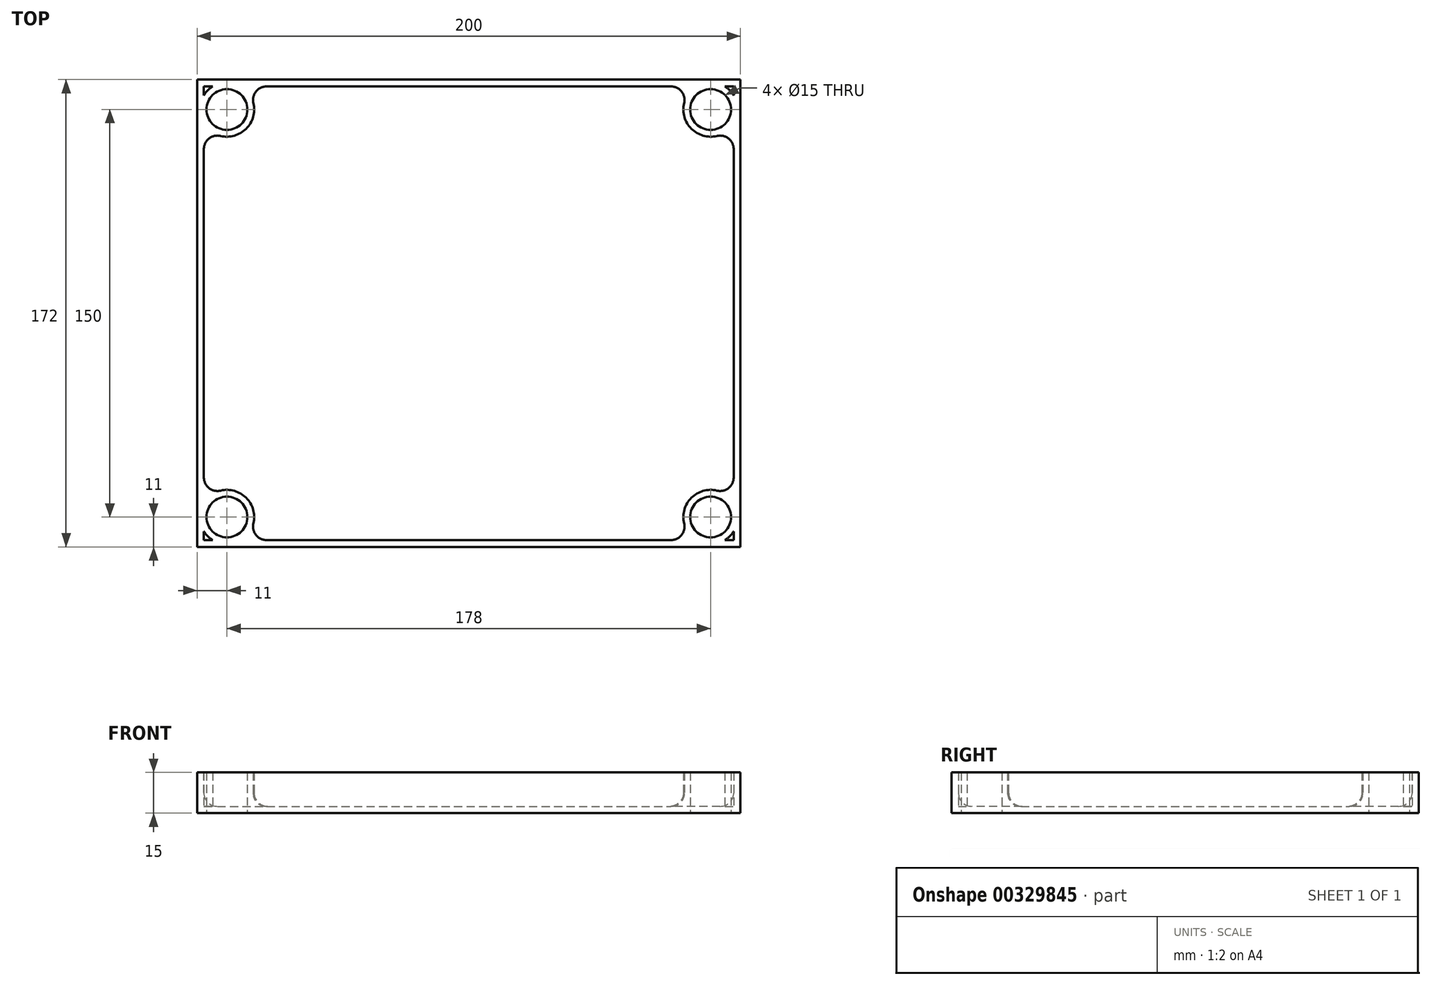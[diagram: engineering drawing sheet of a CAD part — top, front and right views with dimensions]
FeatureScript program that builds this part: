
annotation { "Feature Type Name" : "Feature", "Feature Type Description" : "" }
export const myFeature = defineFeature(function(context is Context, id is Id, definition is map)
    precondition{}
    {
        {
            var Q0;
            Q0=qCreatedBy(makeId("Top.planeOp"),FACE);
            var sketch = newSketch(context, id + "F0", { "sketchPlane" : qUnion([Q0])});
            skLineSegment(sketch, "E0.bottom", {"start": v(0, 0) * mm, "end": v(200, 0) * mm});
            skLineSegment(sketch, "E0.top", {"start": v(0, 172) * mm, "end": v(200, 172) * mm});
            skLineSegment(sketch, "E0.left", {"start": v(0, 0) * mm, "end": v(0, 172) * mm});
            skLineSegment(sketch, "E0.right", {"start": v(200, 0) * mm, "end": v(200, 172) * mm});
            skCircle(sketch, "E1", {"center": v(11, 11) * mm, "radius": 7.5 * mm});
            skCircle(sketch, "E2.0.1.0", {"center": v(11, 161) * mm, "radius": 7.5 * mm});
            skCircle(sketch, "E2.1.0.0", {"center": v(189, 11) * mm, "radius": 7.5 * mm});
            skCircle(sketch, "E2.1.1.0", {"center": v(189, 161) * mm, "radius": 7.5 * mm});
            skLineSegment(sketch, "E2.direction1", {"start": v(11, 11) * mm, "end": v(189, 11) * mm, "construction": true});
            skLineSegment(sketch, "E2.direction2", {"start": v(11, 11) * mm, "end": v(11, 161) * mm, "construction": true});
            skLineSegment(sketch, "E3", {"start": v(0, 11) * mm, "end": v(11, 11) * mm, "construction": true});
            skLineSegment(sketch, "E4", {"start": v(11, 11) * mm, "end": v(11, 0) * mm, "construction": true});
            skLineSegment(sketch, "E5", {"start": v(189, 172) * mm, "end": v(189, 161) * mm, "construction": true});
            skLineSegment(sketch, "E6", {"start": v(189, 161) * mm, "end": v(200, 161) * mm, "construction": true});
            skSolve(sketch);
        }
        {
            var Q0;
            Q0=makeQuery(id+"F0.imprint","IMPRINT",FACE,{"disambiguationData":[TD([[makeQuery(id+"F0.imprint","IMPRINT",EDGE,{"derivedFrom":sQuery(id+"F0.wireOp",EDGE,"E0.bottom")}),1.0]])]});
            extrude(context, id + "F1", {"entities" : qUnion([Q0]), "depth" : 15 * mm, "offsetDistance" : 25 * mm});
        }
        {
            var Q0;
            Q0=makeQuery(id+"F1.opExtrude","CAP_FACE",FACE,{"disambiguationData":[OSD([sQuery(id+"F0.wireOp",EDGE,"E0.bottom"),sQuery(id+"F0.wireOp",EDGE,"E0.top"),sQuery(id+"F0.wireOp",EDGE,"E0.left"),sQuery(id+"F0.wireOp",EDGE,"E0.right"),sQuery(id+"F0.wireOp",EDGE,"E1"),sQuery(id+"F0.wireOp",EDGE,"E2.0.1.0"),sQuery(id+"F0.wireOp",EDGE,"E2.1.0.0"),sQuery(id+"F0.wireOp",EDGE,"E2.1.1.0")])],"isStart":false});
            shell(context, id + "F2", {"entities" : qUnion([Q0]), "thickness" : 2.5 * mm});
        }
        {
            var Q0;
            {var subQ0=sQuery(id+"F0.wireOp",EDGE,"E2.0.1.0");Q0=makeQuery(id+"F2.opShell","OFFSET_EDGE",EDGE,{"disambiguationData":[OSD([subQ0]),TDD([makeQuery(id+"F1.opExtrude","CAP_EDGE",EDGE,{"disambiguationData":[OSD([subQ0])],"isStart":true})]),OD(0.0)]});}
            var Q1;
            {var subQ0=sQuery(id+"F0.wireOp",EDGE,"E2.1.1.0");Q1=makeQuery(id+"F2.opShell","OFFSET_EDGE",EDGE,{"disambiguationData":[OSD([subQ0]),TDD([makeQuery(id+"F1.opExtrude","CAP_EDGE",EDGE,{"disambiguationData":[OSD([subQ0])],"isStart":true})]),OD(0.0)]});}
            var Q2;
            {var subQ0=sQuery(id+"F0.wireOp",EDGE,"E2.1.0.0");Q2=makeQuery(id+"F2.opShell","OFFSET_EDGE",EDGE,{"disambiguationData":[OSD([subQ0]),TDD([makeQuery(id+"F1.opExtrude","CAP_EDGE",EDGE,{"disambiguationData":[OSD([subQ0])],"isStart":true})]),OD(0.0)]});}
            var Q3;
            {var subQ0=sQuery(id+"F0.wireOp",EDGE,"E1");Q3=makeQuery(id+"F2.opShell","OFFSET_EDGE",EDGE,{"disambiguationData":[OSD([subQ0]),TDD([makeQuery(id+"F1.opExtrude","CAP_EDGE",EDGE,{"disambiguationData":[OSD([subQ0])],"isStart":true})]),OD(0.0)]});}
            var Q4;
            {var subQ0=sQuery(id+"F0.wireOp",EDGE,"E0.bottom");Q4=makeQuery(id+"F2.opShell","OFFSET_EDGE",EDGE,{"disambiguationData":[OSD([subQ0]),TDD([makeQuery(id+"F1.opExtrude","CAP_EDGE",EDGE,{"disambiguationData":[OSD([subQ0])],"isStart":true})]),OD(2.0)]});}
            var Q5;
            {var subQ0=sQuery(id+"F0.wireOp",EDGE,"E0.left");Q5=makeQuery(id+"F2.opShell","OFFSET_EDGE",EDGE,{"disambiguationData":[OSD([subQ0]),TDD([makeQuery(id+"F1.opExtrude","CAP_EDGE",EDGE,{"disambiguationData":[OSD([subQ0])],"isStart":true})]),OD(2.0)]});}
            var Q6;
            {var subQ0=sQuery(id+"F0.wireOp",EDGE,"E0.top");Q6=makeQuery(id+"F2.opShell","OFFSET_EDGE",EDGE,{"disambiguationData":[OSD([subQ0]),TDD([makeQuery(id+"F1.opExtrude","CAP_EDGE",EDGE,{"disambiguationData":[OSD([subQ0])],"isStart":true})]),OD(2.0)]});}
            var Q7;
            {var subQ0=sQuery(id+"F0.wireOp",EDGE,"E0.right");Q7=makeQuery(id+"F2.opShell","OFFSET_EDGE",EDGE,{"disambiguationData":[OSD([subQ0]),TDD([makeQuery(id+"F1.opExtrude","CAP_EDGE",EDGE,{"disambiguationData":[OSD([subQ0])],"isStart":true})]),OD(2.0)]});}
            var Q8;
            Q8=makeQuery(id+"F2.opShell","TWEAK_EDGE",EDGE,{"disambiguationData":[OD(1.0)],"derivedFrom":[makeQuery(id+"F1.opExtrude","SWEPT_FACE",FACE,{"disambiguationData":[OSD([sQuery(id+"F0.wireOp",EDGE,"E0.top")])]}),makeQuery(id+"F1.opExtrude","SWEPT_FACE",FACE,{"disambiguationData":[OSD([sQuery(id+"F0.wireOp",EDGE,"E2.0.1.0")])]})]});
            var Q9;
            Q9=makeQuery(id+"F2.opShell","TWEAK_EDGE",EDGE,{"disambiguationData":[OD(1.0)],"derivedFrom":[makeQuery(id+"F1.opExtrude","SWEPT_FACE",FACE,{"disambiguationData":[OSD([sQuery(id+"F0.wireOp",EDGE,"E0.left")])]}),makeQuery(id+"F1.opExtrude","SWEPT_FACE",FACE,{"disambiguationData":[OSD([sQuery(id+"F0.wireOp",EDGE,"E2.0.1.0")])]})]});
            var Q10;
            Q10=makeQuery(id+"F2.opShell","TWEAK_EDGE",EDGE,{"disambiguationData":[OD(1.0)],"derivedFrom":[makeQuery(id+"F1.opExtrude","SWEPT_FACE",FACE,{"disambiguationData":[OSD([sQuery(id+"F0.wireOp",EDGE,"E0.bottom")])]}),makeQuery(id+"F1.opExtrude","SWEPT_FACE",FACE,{"disambiguationData":[OSD([sQuery(id+"F0.wireOp",EDGE,"E1")])]})]});
            var Q11;
            Q11=makeQuery(id+"F2.opShell","TWEAK_EDGE",EDGE,{"disambiguationData":[OD(1.0)],"derivedFrom":[makeQuery(id+"F1.opExtrude","SWEPT_FACE",FACE,{"disambiguationData":[OSD([sQuery(id+"F0.wireOp",EDGE,"E0.left")])]}),makeQuery(id+"F1.opExtrude","SWEPT_FACE",FACE,{"disambiguationData":[OSD([sQuery(id+"F0.wireOp",EDGE,"E1")])]})]});
            var Q12;
            Q12=makeQuery(id+"F2.opShell","TWEAK_EDGE",EDGE,{"disambiguationData":[OD(1.0)],"derivedFrom":[makeQuery(id+"F1.opExtrude","SWEPT_FACE",FACE,{"disambiguationData":[OSD([sQuery(id+"F0.wireOp",EDGE,"E0.bottom")])]}),makeQuery(id+"F1.opExtrude","SWEPT_FACE",FACE,{"disambiguationData":[OSD([sQuery(id+"F0.wireOp",EDGE,"E2.1.0.0")])]})]});
            var Q13;
            Q13=makeQuery(id+"F2.opShell","TWEAK_EDGE",EDGE,{"disambiguationData":[OD(1.0)],"derivedFrom":[makeQuery(id+"F1.opExtrude","SWEPT_FACE",FACE,{"disambiguationData":[OSD([sQuery(id+"F0.wireOp",EDGE,"E0.right")])]}),makeQuery(id+"F1.opExtrude","SWEPT_FACE",FACE,{"disambiguationData":[OSD([sQuery(id+"F0.wireOp",EDGE,"E2.1.0.0")])]})]});
            var Q14;
            Q14=makeQuery(id+"F2.opShell","TWEAK_EDGE",EDGE,{"disambiguationData":[OD(1.0)],"derivedFrom":[makeQuery(id+"F1.opExtrude","SWEPT_FACE",FACE,{"disambiguationData":[OSD([sQuery(id+"F0.wireOp",EDGE,"E0.top")])]}),makeQuery(id+"F1.opExtrude","SWEPT_FACE",FACE,{"disambiguationData":[OSD([sQuery(id+"F0.wireOp",EDGE,"E2.1.1.0")])]})]});
            var Q15;
            Q15=makeQuery(id+"F2.opShell","TWEAK_EDGE",EDGE,{"disambiguationData":[OD(1.0)],"derivedFrom":[makeQuery(id+"F1.opExtrude","SWEPT_FACE",FACE,{"disambiguationData":[OSD([sQuery(id+"F0.wireOp",EDGE,"E0.right")])]}),makeQuery(id+"F1.opExtrude","SWEPT_FACE",FACE,{"disambiguationData":[OSD([sQuery(id+"F0.wireOp",EDGE,"E2.1.1.0")])]})]});
            fillet(context, id + "F3", {"entities" : qUnion([Q0, Q1, Q2, Q3, Q4, Q5, Q6, Q7, Q8, Q9, Q10, Q11, Q12, Q13, Q14, Q15]), "radius" : 5 * mm, "tangentPropagation" : true, "allowEdgeOverflow" : false});
        }
    });
